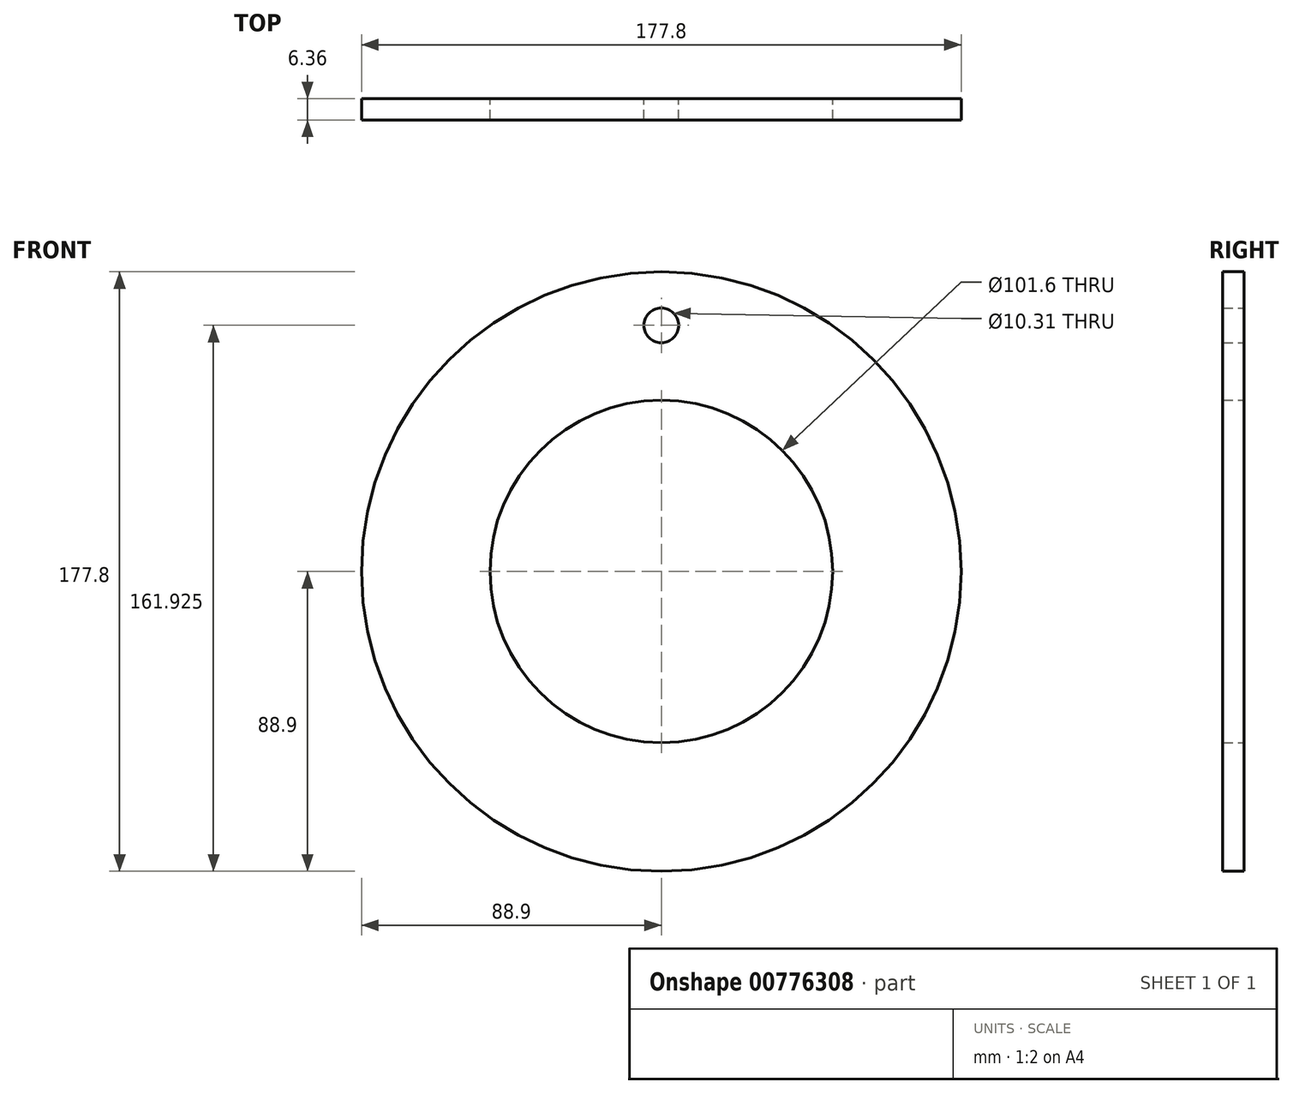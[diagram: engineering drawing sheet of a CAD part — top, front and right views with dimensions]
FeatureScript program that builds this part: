
annotation { "Feature Type Name" : "Feature", "Feature Type Description" : "" }
export const myFeature = defineFeature(function(context is Context, id is Id, definition is map)
    precondition{}
    {
        {
            var Q0;
            Q0=qCreatedBy(makeId("Front.planeOp"),FACE);
            var sketch = newSketch(context, id + "F0", { "sketchPlane" : qUnion([Q0])});
            skCircle(sketch, "E0", {"center": v(0, 0) * mm, "radius": 88.9 * mm});
            skCircle(sketch, "E1", {"center": v(0, 0) * mm, "radius": 50.8 * mm});
            skLineSegment(sketch, "E2", {"start": v(0, 88.9) * mm, "end": v(0, 73.03) * mm});
            skCircle(sketch, "E3", {"center": v(0, 73.03) * mm, "radius": 5.16 * mm});
            skLineSegment(sketch, "E4", {"start": v(0, 0) * mm, "end": v(21.23, 0) * mm});
            skLineSegment(sketch, "E5", {"start": v(0, 0) * mm, "end": v(0, 17.26) * mm});
            skSolve(sketch);
        }
        {
            var Q0;
            Q0=makeQuery(id+"F0.imprint","IMPRINT",FACE,{"disambiguationData":[TD([[makeQuery(id+"F0.imprint","IMPRINT",EDGE,{"derivedFrom":sQuery(id+"F0.wireOp",EDGE,"E0")}),1.0]])]});
            extrude(context, id + "F1", {"entities" : qUnion([Q0]), "endBound" : BoundingType.SYMMETRIC, "depth" : 6.35 * mm, "offsetDistance" : 25.4 * mm});
        }
    });
